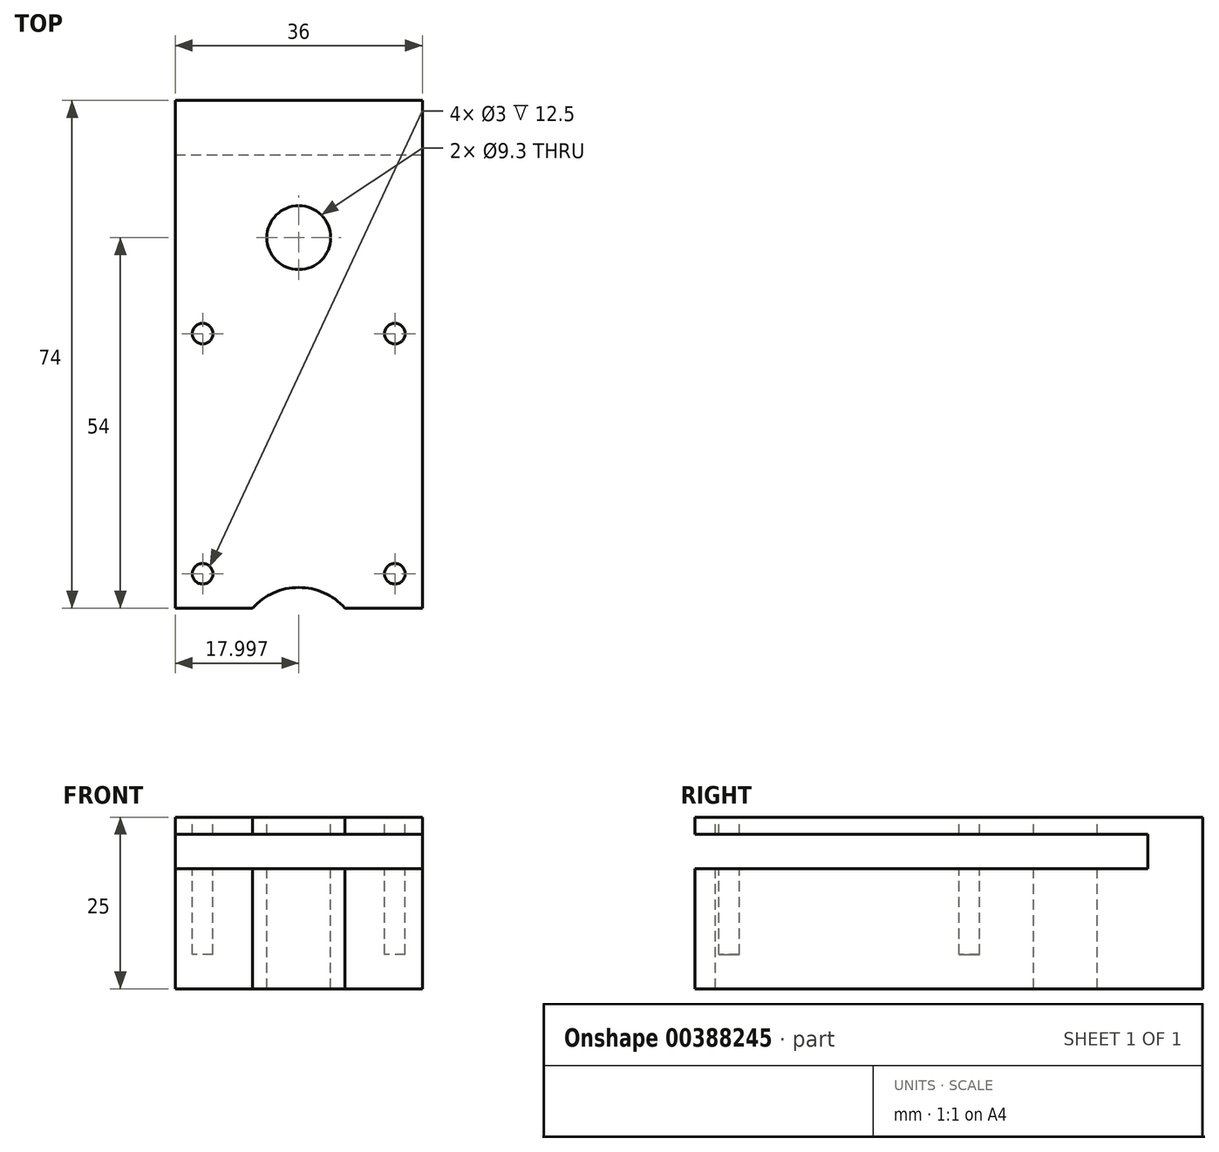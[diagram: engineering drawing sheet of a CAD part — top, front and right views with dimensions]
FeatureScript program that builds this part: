
annotation { "Feature Type Name" : "Feature", "Feature Type Description" : "" }
export const myFeature = defineFeature(function(context is Context, id is Id, definition is map)
    precondition{}
    {
        {
            var Q0;
            Q0=qCreatedBy(makeId("Front.planeOp"),FACE);
            var sketch = newSketch(context, id + "F0", { "sketchPlane" : qUnion([Q0])});
            skLineSegment(sketch, "E0.bottom", {"start": v(-25.44, 17.24) * mm, "end": v(10.56, 17.24) * mm});
            skLineSegment(sketch, "E0.top", {"start": v(-25.44, -7.76) * mm, "end": v(10.56, -7.76) * mm});
            skLineSegment(sketch, "E0.left", {"start": v(-25.44, 17.24) * mm, "end": v(-25.44, -7.76) * mm});
            skLineSegment(sketch, "E0.right", {"start": v(10.56, 17.24) * mm, "end": v(10.56, -7.76) * mm});
            skSolve(sketch);
        }
        {
            var Q0;
            Q0=makeQuery(id+"F0.imprint","IMPRINT",FACE,{"disambiguationData":[TD([[makeQuery(id+"F0.imprint","IMPRINT",EDGE,{"derivedFrom":sQuery(id+"F0.wireOp",EDGE,"E0.bottom")}),-1.0]])]});
            extrude(context, id + "F1", {"entities" : qUnion([Q0]), "depth" : 80 * mm});
        }
        {
            var Q0;
            Q0=makeQuery(id+"F1.opExtrude","SWEPT_FACE",FACE,{"disambiguationData":[OSD([sQuery(id+"F0.wireOp",EDGE,"E0.bottom")])]});
            var sketch = newSketch(context, id + "F2", { "sketchPlane" : qUnion([Q0])});
            skArc(sketch, "E1", {"start": v(1.56, -80) * mm, "mid": v(-7.44, -71) * mm, "end": v(-16.44, -80) * mm});
            skPoint(sketch, "E2.end.orphan", {"position": v(-7.44, -71) * mm});
            skLineSegment(sketch, "E3", {"start": v(-16.44, -80) * mm, "end": v(1.56, -80) * mm});
            skSolve(sketch);
        }
        {
            var Q0;
            Q0=makeQuery(id+"F2.imprint","IMPRINT",FACE,{"disambiguationData":[TD([[makeQuery(id+"F2.imprint","IMPRINT",EDGE,{"derivedFrom":sQuery(id+"F2.wireOp",EDGE,"E1")}),1.0]])]});
            extrude(context, id + "F3", {"entities" : qUnion([Q0]), "operationType" : NewBodyOperationType.REMOVE, "oppositeDirection" : true, "depth" : 25 * mm});
        }
        {
            var Q0;
            Q0=makeQuery(id+"F1.opExtrude","SWEPT_FACE",FACE,{"disambiguationData":[OSD([sQuery(id+"F0.wireOp",EDGE,"E0.bottom")])]});
            var sketch = newSketch(context, id + "F4", { "sketchPlane" : qUnion([Q0])});
            skCircle(sketch, "E4", {"center": v(-7.44, -20) * mm, "radius": 4.65 * mm});
            skPoint(sketch, "E4.centerSnap0", {"position": v(-7.44, -71) * mm});
            skLineSegment(sketch, "E5", {"start": v(-16.44, -80) * mm, "end": v(1.56, -80) * mm});
            skSolve(sketch);
        }
        {
            var Q0;
            Q0=makeQuery(id+"F4.imprint","IMPRINT",FACE,{"disambiguationData":[TD([[makeQuery(id+"F4.imprint","IMPRINT",EDGE,{"derivedFrom":sQuery(id+"F4.wireOp",EDGE,"E4")}),1.0]])]});
            var Q1;
            Q1=sQuery(id+"F4.wireOp",EDGE,"E4");
            extrude(context, id + "F5", {"entities" : qUnion([Q0]), "operationType" : NewBodyOperationType.REMOVE, "surfaceEntities" : qUnion([Q1]), "oppositeDirection" : true, "depth" : 25 * mm});
        }
        {
            var Q0;
            {var subQ0=sQuery(id+"F0.wireOp",EDGE,"E0.bottom");var subQ1=sQuery(id+"F0.wireOp",EDGE,"E0.top");var subQ2=sQuery(id+"F0.wireOp",EDGE,"E0.left");Q0=makeQuery(id+"F3.boolean.opBoolean","SPLIT",FACE,{"disambiguationData":[TD([makeQuery(id+"F1.opExtrude","SWEPT_FACE",FACE,{"disambiguationData":[OSD([subQ2])]})])],"derivedFrom":makeQuery(id+"F1.opExtrude","CAP_FACE",FACE,{"disambiguationData":[OSD([subQ0,subQ1,subQ2,sQuery(id+"F0.wireOp",EDGE,"E0.right")])],"isStart":false})});}
            var sketch = newSketch(context, id + "F6", { "sketchPlane" : qUnion([Q0])});
            skLineSegment(sketch, "E6", {"start": v(-25.44, 9.74) * mm, "end": v(-25.44, 14.74) * mm});
            skLineSegment(sketch, "E7", {"start": v(-25.44, 14.74) * mm, "end": v(10.56, 14.74) * mm});
            skLineSegment(sketch, "E8", {"start": v(10.56, 14.74) * mm, "end": v(10.56, 9.74) * mm});
            skLineSegment(sketch, "E9", {"start": v(10.56, 9.74) * mm, "end": v(-25.44, 9.74) * mm});
            skSolve(sketch);
        }
        {
            var Q0;
            {var subQ0=sQuery(id+"F6.wireOp",EDGE,"E6");Q0=makeQuery(id+"F6.imprint","IMPRINT",FACE,{"disambiguationData":[TD([[makeQuery(id+"F6.imprint","IMPRINT",EDGE,{"derivedFrom":subQ0}),1.0]])]});}
            var Q1;
            {var subQ0=sQuery(id+"F6.wireOp",EDGE,"E8");Q1=makeQuery(id+"F6.imprint","IMPRINT",FACE,{"disambiguationData":[TD([[makeQuery(id+"F6.imprint","IMPRINT",EDGE,{"derivedFrom":subQ0}),-1.0]])]});}
            extrude(context, id + "F7", {"entities" : qUnion([Q0, Q1]), "operationType" : NewBodyOperationType.REMOVE, "oppositeDirection" : true, "depth" : 72 * mm});
        }
        {
            var Q0;
            {var subQ0=sQuery(id+"F0.wireOp",EDGE,"E0.bottom");var subQ1=makeQuery(id+"F1.opExtrude","SWEPT_FACE",FACE,{"disambiguationData":[OSD([subQ0])]});var subQ2=sQuery(id+"F0.wireOp",EDGE,"E0.left");var subQ3=makeQuery(id+"F1.opExtrude","SWEPT_FACE",FACE,{"disambiguationData":[OSD([subQ2])]});var subQ5=sQuery(id+"F0.wireOp",EDGE,"E0.top");Q0=makeQuery(id+"F7.boolean.opBoolean","SPLIT",FACE,{"disambiguationData":[TD([subQ1])],"derivedFrom":makeQuery(id+"F3.boolean.opBoolean","SPLIT",FACE,{"disambiguationData":[TD([subQ3])],"derivedFrom":makeQuery(id+"F1.opExtrude","CAP_FACE",FACE,{"disambiguationData":[OSD([subQ0,subQ5,subQ2,sQuery(id+"F0.wireOp",EDGE,"E0.right")])],"isStart":false})})});}
            var sketch = newSketch(context, id + "F8", { "sketchPlane" : qUnion([Q0])});
            skLineSegment(sketch, "E10", {"start": v(-25.44, 17.24) * mm, "end": v(10.56, 17.24) * mm});
            skLineSegment(sketch, "E11", {"start": v(10.56, 17.24) * mm, "end": v(10.56, 14.74) * mm});
            skLineSegment(sketch, "E12", {"start": v(10.56, 14.74) * mm, "end": v(-25.44, 14.74) * mm});
            skLineSegment(sketch, "E13", {"start": v(-25.44, 14.74) * mm, "end": v(-25.44, 17.24) * mm});
            skSolve(sketch);
        }
        {
            var Q0;
            Q0 = qSketchRegion(id + "F8", true);
            extrude(context, id + "F9", {"entities" : qUnion([Q0]), "operationType" : NewBodyOperationType.REMOVE, "oppositeDirection" : true, "depth" : 6 * mm});
        }
        {
            var Q0;
            {var subQ0=sQuery(id+"F0.wireOp",EDGE,"E0.top");var subQ1=makeQuery(id+"F1.opExtrude","SWEPT_FACE",FACE,{"disambiguationData":[OSD([subQ0])]});var subQ2=sQuery(id+"F0.wireOp",EDGE,"E0.left");var subQ3=makeQuery(id+"F1.opExtrude","SWEPT_FACE",FACE,{"disambiguationData":[OSD([subQ2])]});var subQ5=sQuery(id+"F0.wireOp",EDGE,"E0.bottom");Q0=makeQuery(id+"F7.boolean.opBoolean","SPLIT",FACE,{"disambiguationData":[TD([subQ1])],"derivedFrom":makeQuery(id+"F3.boolean.opBoolean","SPLIT",FACE,{"disambiguationData":[TD([subQ3])],"derivedFrom":makeQuery(id+"F1.opExtrude","CAP_FACE",FACE,{"disambiguationData":[OSD([subQ5,subQ0,subQ2,sQuery(id+"F0.wireOp",EDGE,"E0.right")])],"isStart":false})})});}
            var sketch = newSketch(context, id + "F10", { "sketchPlane" : qUnion([Q0])});
            skLineSegment(sketch, "E14", {"start": v(-25.44, 9.74) * mm, "end": v(10.56, 9.74) * mm});
            skPoint(sketch, "E14.endSnap0", {"position": v(-20.94, 9.74) * mm});
            skLineSegment(sketch, "E15", {"start": v(10.56, 9.74) * mm, "end": v(10.56, -7.76) * mm});
            skLineSegment(sketch, "E16", {"start": v(10.56, -7.76) * mm, "end": v(-25.44, -7.76) * mm});
            skLineSegment(sketch, "E17", {"start": v(-25.44, -7.76) * mm, "end": v(-25.44, 9.74) * mm});
            skSolve(sketch);
        }
        {
            var Q0;
            Q0 = qSketchRegion(id + "F10", true);
            extrude(context, id + "F11", {"entities" : qUnion([Q0]), "operationType" : NewBodyOperationType.REMOVE, "oppositeDirection" : true, "depth" : 6 * mm});
        }
        {
            var Q0;
            Q0=makeQuery(id+"F1.opExtrude","SWEPT_FACE",FACE,{"disambiguationData":[OSD([sQuery(id+"F0.wireOp",EDGE,"E0.bottom")])]});
            var sketch = newSketch(context, id + "F12", { "sketchPlane" : qUnion([Q0])});
            skLineSegment(sketch, "E18", {"start": v(-7.44, -71) * mm, "end": v(-7.44, -18.82) * mm});
            skCircle(sketch, "E19", {"center": v(-21.44, -69) * mm, "radius": 1.5 * mm});
            skCircle(sketch, "E20", {"center": v(-21.44, -34) * mm, "radius": 1.5 * mm});
            skCircle(sketch, "E21", {"center": v(6.56, -34) * mm, "radius": 1.5 * mm});
            skCircle(sketch, "E22", {"center": v(6.56, -69) * mm, "radius": 1.5 * mm});
            skSolve(sketch);
        }
        {
            var Q0;
            Q0 = qSketchRegion(id + "F12", true);
            extrude(context, id + "F13", {"entities" : qUnion([Q0]), "operationType" : NewBodyOperationType.REMOVE, "oppositeDirection" : true, "depth" : 20 * mm});
        }
    });
